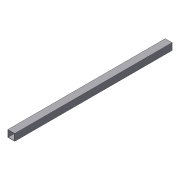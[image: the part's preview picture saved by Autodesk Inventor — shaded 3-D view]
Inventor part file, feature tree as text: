
AUTODESK INVENTOR PART (.ipt)
format: ipt  version: 2012 (Build 160160000, 160)  size: 71,168 bytes
history: native  units: in
note: dims shown in document units (in); Inventor stores cm internally (conversion verified against a paired STEP export)
features: extrude x1, shell x1, sketch x1
ambient origin geometry x8: Origin, YZ Plane, XZ Plane, XY Plane, X Axis, Y Axis, Z Axis, Center Point
bodies: Solid1 (feature_tree)
feature tree (3):
  extrude  "Extrusion1"  Depth=1.0in
  shell  "Shell1"  Thickness=23.0in
  sketch  "Sketch1"  dims[d0=1.0in d1=1.0in d2=23.0in d3=0.0in d4=0.0625in]
